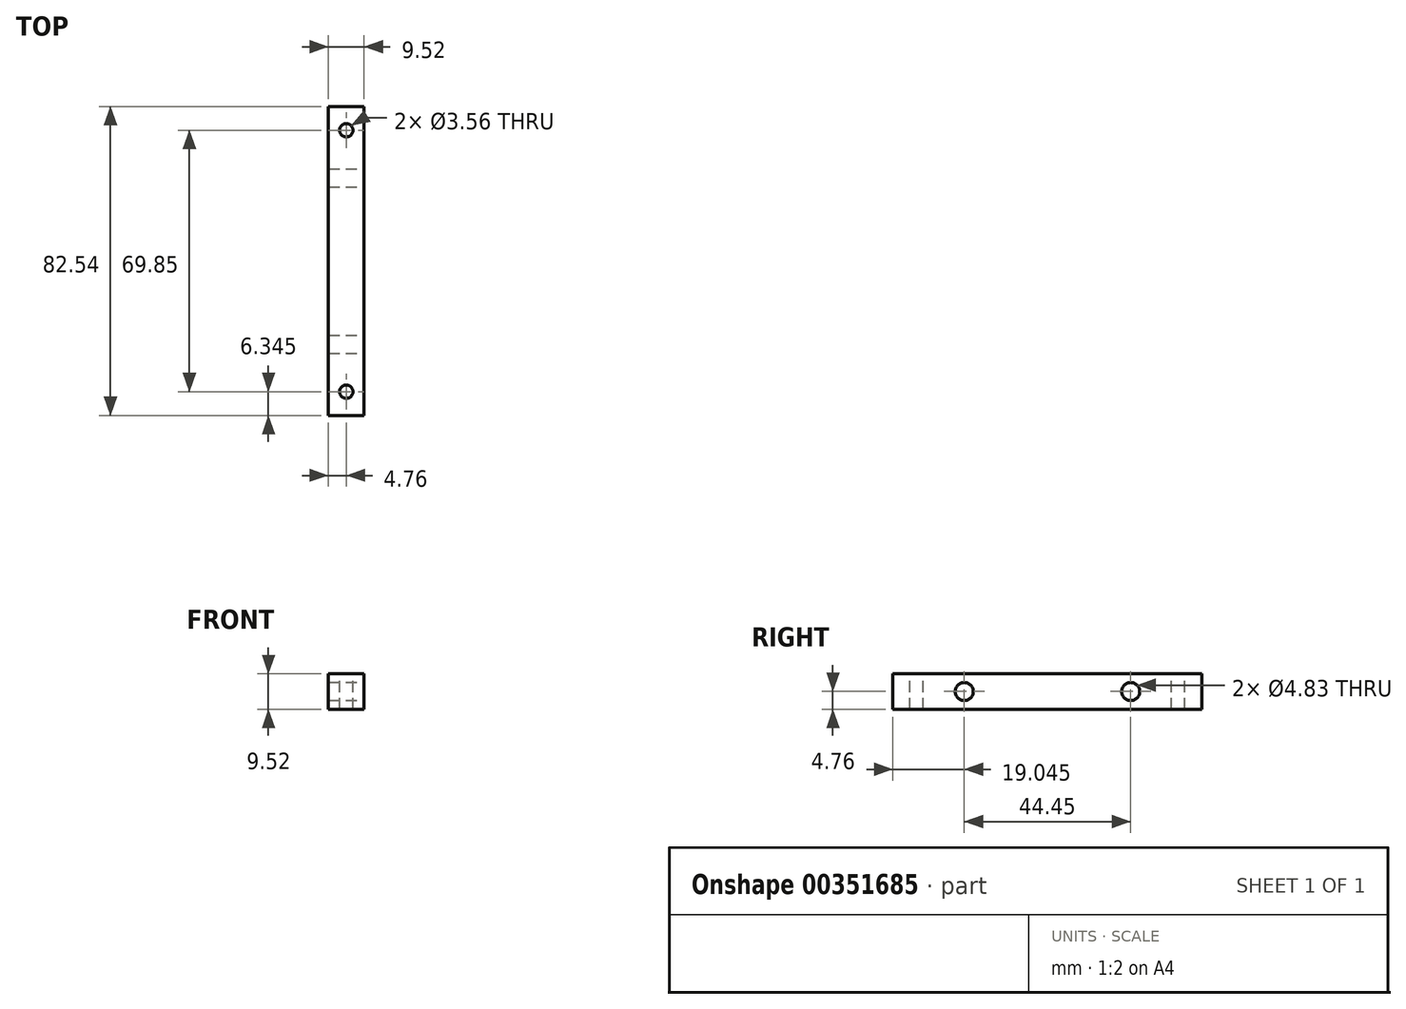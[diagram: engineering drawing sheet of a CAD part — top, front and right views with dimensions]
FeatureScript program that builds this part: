
annotation { "Feature Type Name" : "Feature", "Feature Type Description" : "" }
export const myFeature = defineFeature(function(context is Context, id is Id, definition is map)
    precondition{}
    {
        {
            var Q0;
            Q0=qCreatedBy(makeId("Front.planeOp"),FACE);
            var sketch = newSketch(context, id + "F0", { "sketchPlane" : qUnion([Q0])});
            skLineSegment(sketch, "E0.bottom", {"start": v(-4.76, 4.76) * mm, "end": v(4.76, 4.76) * mm});
            skLineSegment(sketch, "E0.top", {"start": v(-4.76, -4.76) * mm, "end": v(4.76, -4.76) * mm});
            skLineSegment(sketch, "E0.left", {"start": v(-4.76, 4.76) * mm, "end": v(-4.76, -4.76) * mm});
            skLineSegment(sketch, "E0.right", {"start": v(4.76, 4.76) * mm, "end": v(4.76, -4.76) * mm});
            skPoint(sketch, "E0.middle", {"position": v(0, 0) * mm});
            skSolve(sketch);
        }
        {
            var Q0;
            Q0 = qSketchRegion(id + "F0", true);
            extrude(context, id + "F1", {"entities" : qUnion([Q0]), "endBound" : BoundingType.SYMMETRIC, "depth" : 82.55 * mm});
        }
        {
            var Q0;
            Q0=makeQuery(id+"F1.opExtrude","SWEPT_FACE",FACE,{"disambiguationData":[OSD([sQuery(id+"F0.wireOp",EDGE,"E0.bottom")])]});
            var sketch = newSketch(context, id + "F2", { "sketchPlane" : qUnion([Q0])});
            skCircle(sketch, "E1", {"center": v(0, -34.93) * mm, "radius": 1.78 * mm});
            skCircle(sketch, "E2", {"center": v(0, 34.93) * mm, "radius": 1.78 * mm});
            skSolve(sketch);
        }
        {
            var Q0;
            Q0 = qSketchRegion(id + "F2", true);
            extrude(context, id + "F3", {"entities" : qUnion([Q0]), "operationType" : NewBodyOperationType.REMOVE, "oppositeDirection" : true, "depth" : 9.52 * mm});
        }
        {
            var Q0;
            Q0=makeQuery(id+"F1.opExtrude","SWEPT_FACE",FACE,{"disambiguationData":[OSD([sQuery(id+"F0.wireOp",EDGE,"E0.right")])]});
            var sketch = newSketch(context, id + "F4", { "sketchPlane" : qUnion([Q0])});
            skCircle(sketch, "E3", {"center": v(-22.23, 0) * mm, "radius": 2.41 * mm});
            skCircle(sketch, "E4", {"center": v(22.22, 0) * mm, "radius": 2.41 * mm});
            skSolve(sketch);
        }
        {
            var Q0;
            Q0 = qSketchRegion(id + "F4", true);
            extrude(context, id + "F5", {"entities" : qUnion([Q0]), "operationType" : NewBodyOperationType.REMOVE, "oppositeDirection" : true, "depth" : 9.52 * mm});
        }
    });
